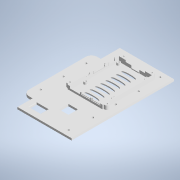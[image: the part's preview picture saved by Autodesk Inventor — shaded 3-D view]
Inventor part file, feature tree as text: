
AUTODESK INVENTOR PART (.ipt)
format: ipt  version: 2022 (Build 260153000, 153)  size: 476,160 bytes
history: native  units: mm
features: reference x13, extrude x9, sketch x9, other x8, fillet x3, projected_geometry x1, imported_body x1
ambient origin geometry x8: Origin, YZ Plane, XZ Plane, XY Plane, X Axis, Y Axis, Z Axis, Center Point
bodies: Body1 (feature_tree)
feature tree (44):
  other  "Твердое тело1"
  extrude  "Выдавливание1"  Depth=10.0mm
  extrude  "Выдавливание2"  Depth=10.0mm
  extrude  "Выдавливание3"  Depth=10.0mm
  extrude  "Выдавливание4"  Depth=13.0mm
  extrude  "Выдавливание5"  Depth=3.5mm TaperAngle=0.0deg
  extrude  "Выдавливание6"  Depth=11.0mm
  extrude  "Выдавливание7"  Depth=11.0mm
  fillet  "Сопряжение1"  Radius=3.5mm
  fillet  "Сопряжение2"  Radius=120.0mm
  extrude  "Выдавливание8"  Depth=30.0mm
  extrude  "Выдавливание9"  Depth=30.0mm
  fillet  "Сопряжение3"  Radius=3.5mm
  sketch  "Эскиз1"
  projected_geometry  "Спроецированная петля1"
  sketch  "Эскиз2"
  reference  "Ссылка1"
  sketch  "Эскиз3"
  sketch  "Эскиз4"
  sketch  "Эскиз5"
  sketch  "Эскиз6"
  sketch  "Эскиз7"
  reference  "Ссылка2"
  reference  "Ссылка3"
  reference  "Ссылка4"
  reference  "Ссылка5"
  reference  "Ссылка6"
  reference  "Ссылка7"
  reference  "Ссылка8"
  sketch  "Эскиз8"
  reference  "Ссылка9"
  reference  "Ссылка10"
  reference  "Ссылка11"
  reference  "Ссылка12"
  reference  "Ссылка13"
  sketch  "Эскиз9"
  imported_body  "БазТело1"
  other  "<path> - Robot.iam"
  other  "000.000 - Robot.iam"
  other  "000.002 - bamper:1"
  other  "000.001 - Bottom:1"
  other  "000.002 - bamper:2"
  other  "01_Крепление_мотора:1"
  other  "01_Крепление_мотора:3"
note: 1 file-system path scrubbed to <path> (originals preserved in map.json)
